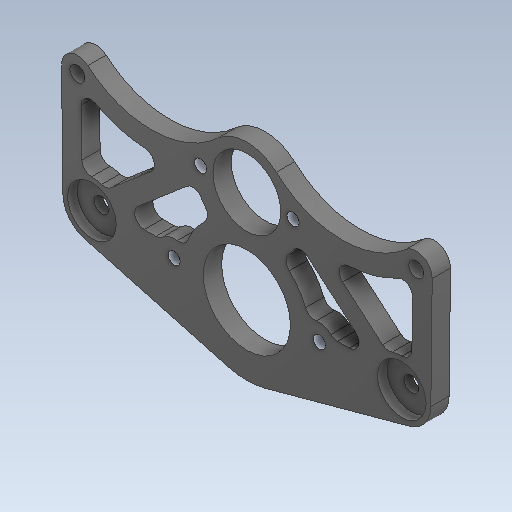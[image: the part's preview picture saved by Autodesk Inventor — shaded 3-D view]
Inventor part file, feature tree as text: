
AUTODESK INVENTOR PART (.ipt)
format: ipt  version: 2020 (Build 240168000, 168)  size: 208,384 bytes
history: native  units: in
note: dims shown in document units (in); Inventor stores cm internally (conversion verified against a paired STEP export)
features: fillet x1
ambient origin geometry x8: Origin, YZ Plane, XZ Plane, XY Plane, X Axis, Y Axis, Z Axis, Center Point
bodies: Solid1 (feature_tree)
feature tree (1):
  fillet  "Fillet2"  [1 undecoded]
note: 1 required parameter value undecoded (feature->parameter linkage not recoverable at this tier; creation-order binding heuristic only, values carry confidence <= 0.55)
